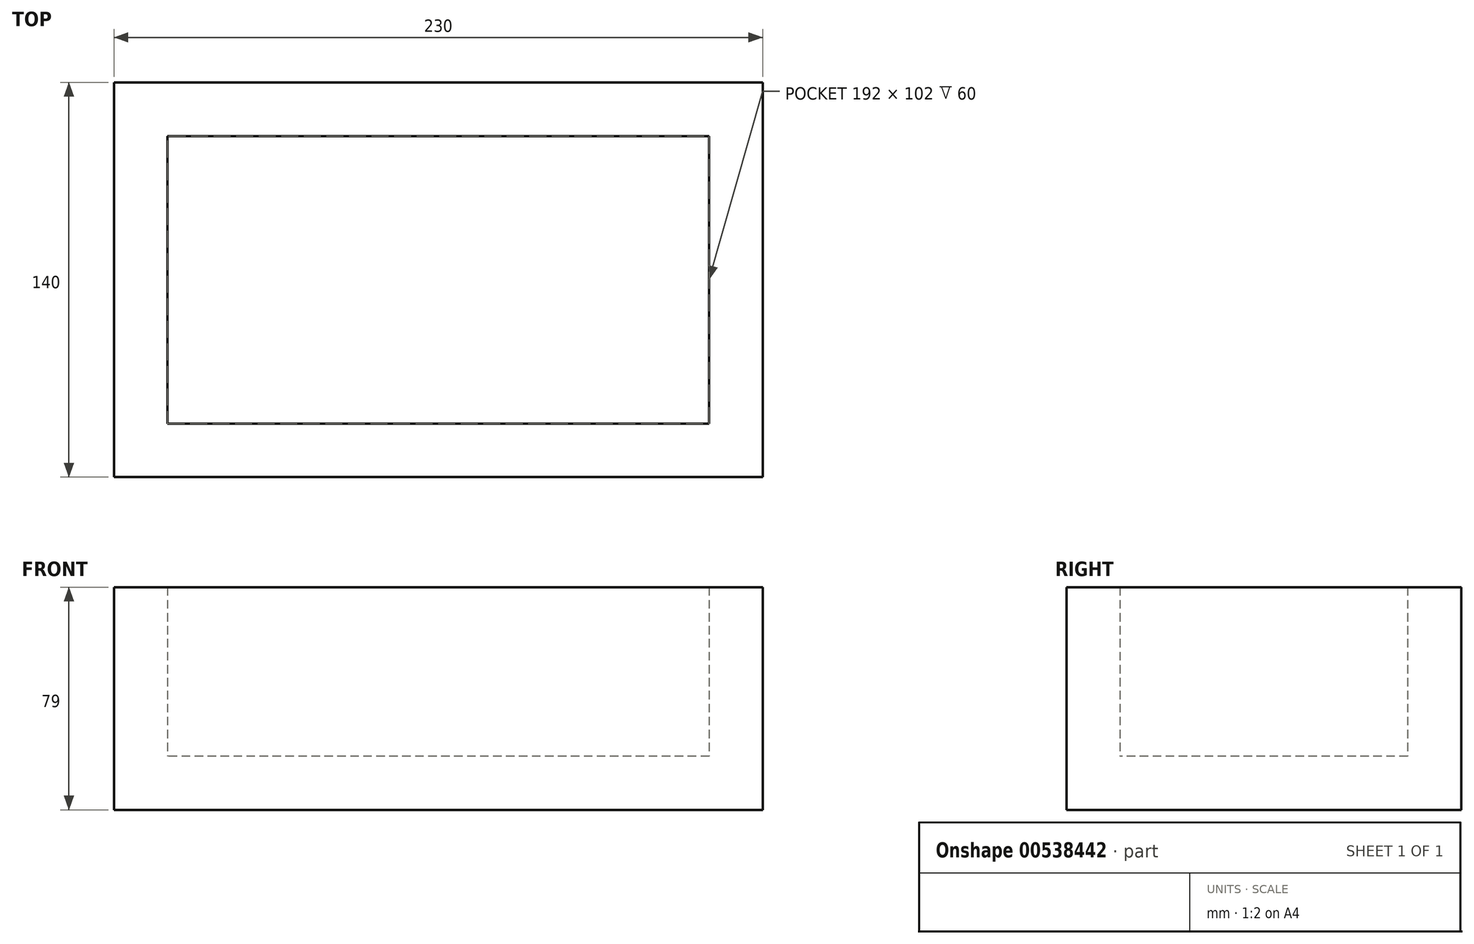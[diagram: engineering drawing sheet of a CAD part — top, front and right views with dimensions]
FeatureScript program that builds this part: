
annotation { "Feature Type Name" : "Feature", "Feature Type Description" : "" }
export const myFeature = defineFeature(function(context is Context, id is Id, definition is map)
    precondition{}
    {
        {
            var Q0;
            Q0=qCreatedBy(makeId("Top.planeOp"),FACE);
            var sketch = newSketch(context, id + "F0", { "sketchPlane" : qUnion([Q0])});
            skLineSegment(sketch, "E0.bottom", {"start": v(115, -75.1) * mm, "end": v(-115, -75.1) * mm});
            skLineSegment(sketch, "E0.top", {"start": v(115, 64.9) * mm, "end": v(-115, 64.9) * mm});
            skLineSegment(sketch, "E0.left", {"start": v(115, -75.1) * mm, "end": v(115, 64.9) * mm});
            skLineSegment(sketch, "E0.right", {"start": v(-115, -75.1) * mm, "end": v(-115, 64.9) * mm});
            skPoint(sketch, "E0.middle", {"position": v(0, -5.1) * mm});
            skSolve(sketch);
        }
        {
            var Q0;
            Q0=makeQuery(id+"F0.imprint","IMPRINT",FACE,{"disambiguationData":[TD([[makeQuery(id+"F0.imprint","IMPRINT",EDGE,{"derivedFrom":sQuery(id+"F0.wireOp",EDGE,"E0.bottom")}),-1.0]])]});
            extrude(context, id + "F1", {"entities" : qUnion([Q0]), "depth" : 19 * mm, "offsetDistance" : 25 * mm});
        }
        {
            var Q0;
            Q0=makeQuery(id+"F1.opExtrude","CAP_FACE",FACE,{"disambiguationData":[OSD([sQuery(id+"F0.wireOp",EDGE,"E0.bottom"),sQuery(id+"F0.wireOp",EDGE,"E0.top"),sQuery(id+"F0.wireOp",EDGE,"E0.left"),sQuery(id+"F0.wireOp",EDGE,"E0.right")])],"isStart":false});
            var sketch = newSketch(context, id + "F2", { "sketchPlane" : qUnion([Q0])});
            skLineSegment(sketch, "E1.bottom", {"start": v(-115, -75.1) * mm, "end": v(115, -75.1) * mm});
            skLineSegment(sketch, "E1.top", {"start": v(-115, 64.9) * mm, "end": v(115, 64.9) * mm});
            skLineSegment(sketch, "E1.left", {"start": v(-115, -75.1) * mm, "end": v(-115, 64.9) * mm});
            skLineSegment(sketch, "E1.right", {"start": v(115, -75.1) * mm, "end": v(115, 64.9) * mm});
            skLineSegment(sketch, "E2.bottom", {"start": v(96, 45.9) * mm, "end": v(-96, 45.9) * mm});
            skLineSegment(sketch, "E2.top", {"start": v(96, -56.1) * mm, "end": v(-96, -56.1) * mm});
            skLineSegment(sketch, "E2.left", {"start": v(96, 45.9) * mm, "end": v(96, -56.1) * mm});
            skLineSegment(sketch, "E2.right", {"start": v(-96, 45.9) * mm, "end": v(-96, -56.1) * mm});
            skPoint(sketch, "E2.middle", {"position": v(0, -5.1) * mm});
            skSolve(sketch);
        }
        {
            var Q0;
            Q0=makeQuery(id+"F2.imprint","IMPRINT",FACE,{"disambiguationData":[TD([[makeQuery(id+"F2.imprint","IMPRINT",EDGE,{"derivedFrom":sQuery(id+"F2.wireOp",EDGE,"E1.bottom")}),-1.0]])]});
            extrude(context, id + "F3", {"entities" : qUnion([Q0]), "operationType" : NewBodyOperationType.ADD, "depth" : 60 * mm, "offsetDistance" : 25 * mm});
        }
    });
